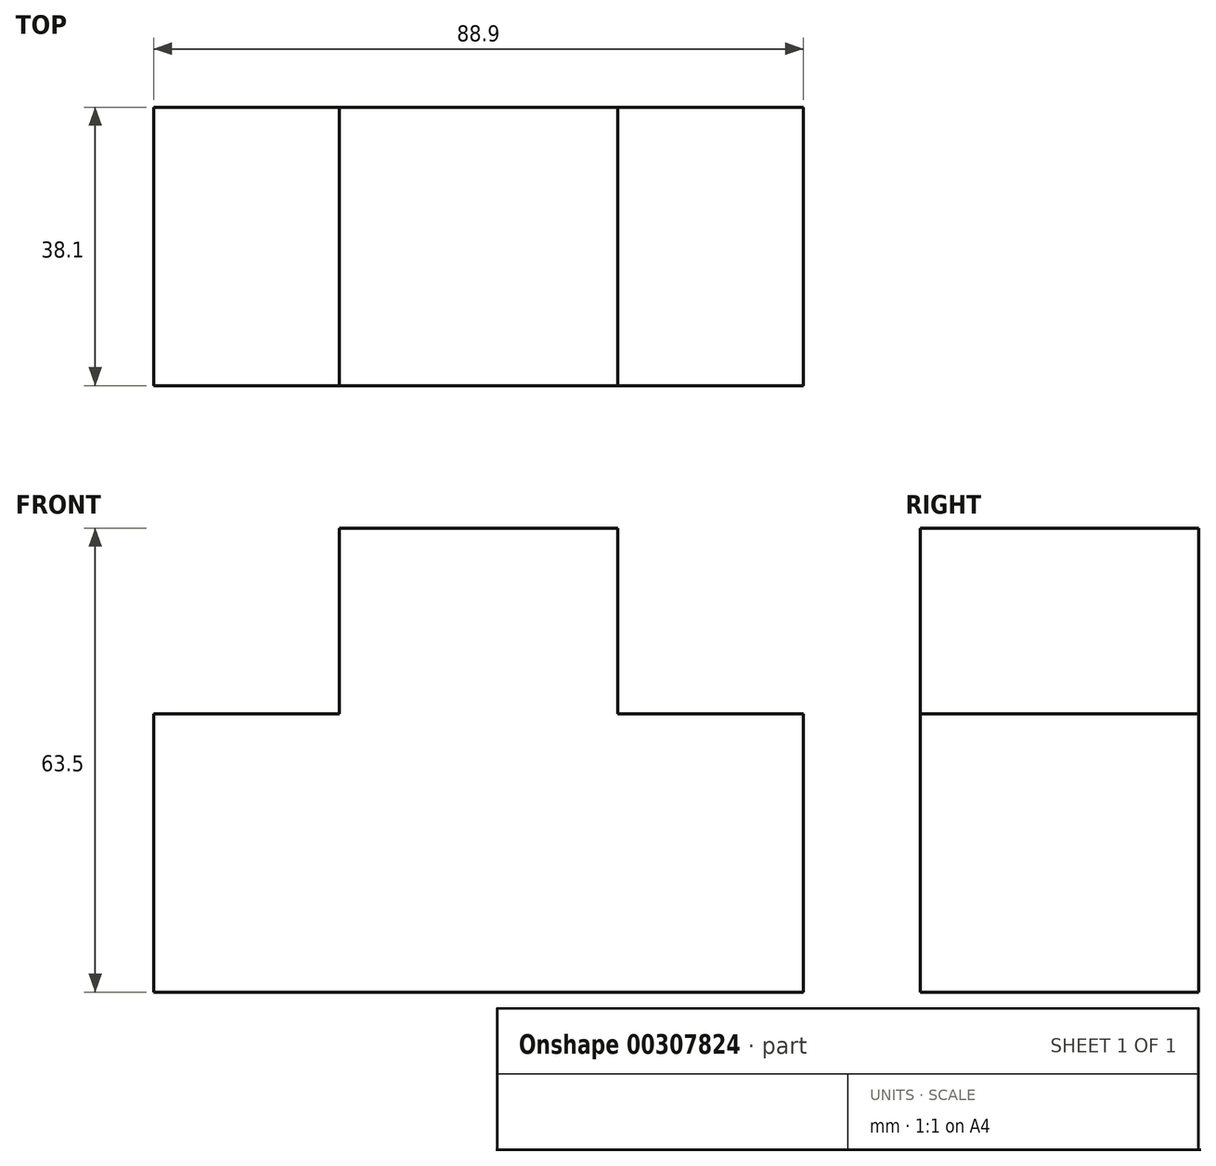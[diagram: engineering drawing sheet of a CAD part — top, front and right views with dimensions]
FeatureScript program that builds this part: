
annotation { "Feature Type Name" : "Feature", "Feature Type Description" : "" }
export const myFeature = defineFeature(function(context is Context, id is Id, definition is map)
    precondition{}
    {
        {
            var Q0;
            Q0=qCreatedBy(makeId("Front.planeOp"),FACE);
            var sketch = newSketch(context, id + "F0", { "sketchPlane" : qUnion([Q0])});
            skLineSegment(sketch, "E0", {"start": v(-53.7, 0.94) * mm, "end": v(-28.3, 0.94) * mm});
            skLineSegment(sketch, "E1", {"start": v(-28.3, 0.94) * mm, "end": v(-28.3, 26.34) * mm});
            skLineSegment(sketch, "E2", {"start": v(-28.3, 26.34) * mm, "end": v(9.8, 26.34) * mm});
            skLineSegment(sketch, "E3", {"start": v(9.8, 26.34) * mm, "end": v(9.8, 0.94) * mm});
            skLineSegment(sketch, "E4", {"start": v(9.8, 0.94) * mm, "end": v(35.2, 0.94) * mm});
            skLineSegment(sketch, "E5", {"start": v(35.2, 0.94) * mm, "end": v(35.2, -37.16) * mm});
            skLineSegment(sketch, "E6", {"start": v(35.2, -37.16) * mm, "end": v(-53.7, -37.16) * mm});
            skLineSegment(sketch, "E7", {"start": v(-53.7, 0.94) * mm, "end": v(-53.7, -37.16) * mm});
            skSolve(sketch);
        }
        {
            var Q0;
            Q0 = qSketchRegion(id + "F0", true);
            extrude(context, id + "F1", {"entities" : qUnion([Q0]), "depth" : 38.1 * mm});
        }
    });
